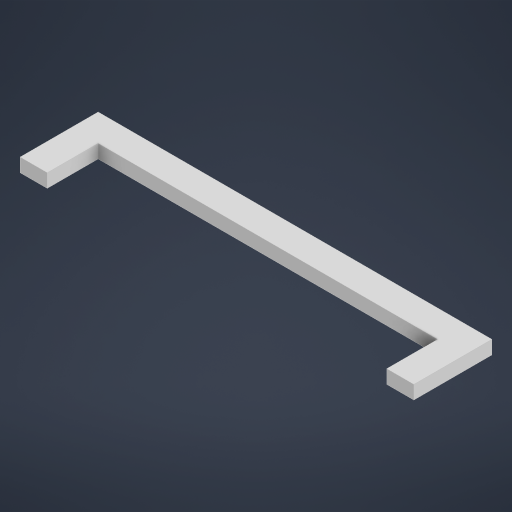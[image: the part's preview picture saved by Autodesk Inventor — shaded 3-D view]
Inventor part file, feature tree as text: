
AUTODESK INVENTOR PART (.ipt)
format: ipt  version: 2023.2 (Build 272271000, 271)  size: 208,896 bytes
history: native  units: mm
features: sketch x1
ambient origin geometry x8: Origin, YZ Plane, XZ Plane, XY Plane, X Axis, Y Axis, Z Axis, Center Point
bodies: Body1 (feature_tree)
feature tree (1):
  sketch  "Sketch1"  dims[d236=4.0mm d237=0.0mm d243=8.0mm d245=100.0mm d246=15.0mm d9=0.5mm d10=0.872665mm d11=0.5mm d12=0.872665mm d13=0.5mm d14=0.872665mm d27=0.5mm d28=0.872665mm d29=0.5mm d30=0.872665mm d88=0.5mm d89=0.872665mm d90=0.5mm d91=0.872665mm d116=0.5mm d117=0.872665mm d118=0.5mm d119=0.872665mm d154=0.5mm d155=0.872665mm d156=0.5mm d157=0.872665mm d181=0.5mm d182=0.872665mm d183=0.5mm d184=0.872665mm d221=0.5mm d222=0.872665mm d223=0.5mm d224=0.872665mm]
